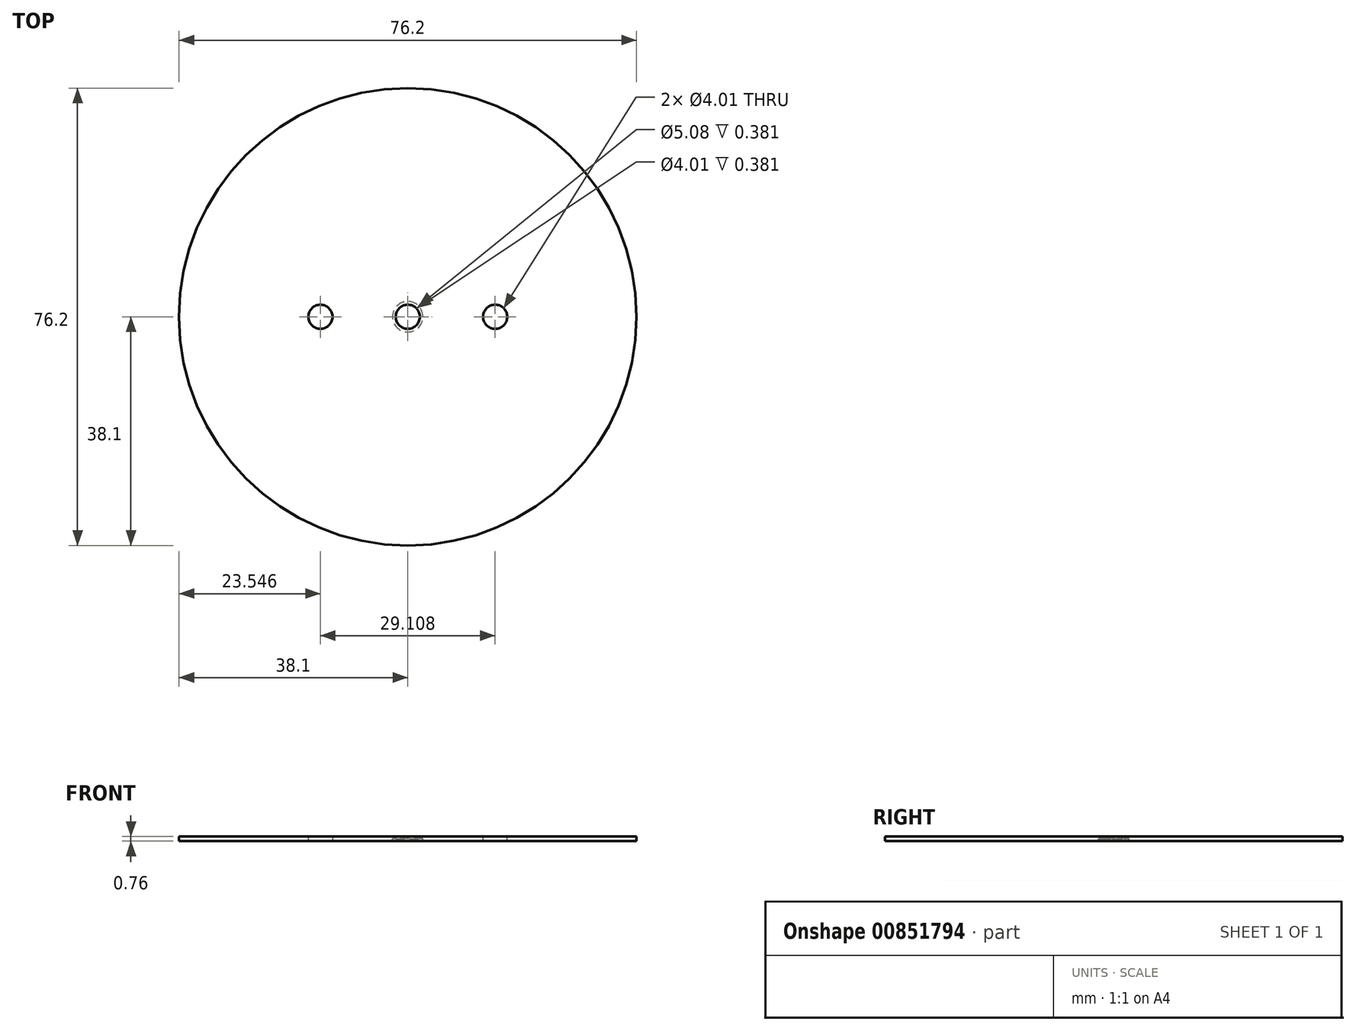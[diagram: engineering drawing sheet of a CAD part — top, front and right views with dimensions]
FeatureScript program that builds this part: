
annotation { "Feature Type Name" : "Feature", "Feature Type Description" : "" }
export const myFeature = defineFeature(function(context is Context, id is Id, definition is map)
    precondition{}
    {
        {
            var Q0;
            Q0=qCreatedBy(makeId("Top.planeOp"),FACE);
            var sketch = newSketch(context, id + "F0", { "sketchPlane" : qUnion([Q0])});
            skCircle(sketch, "E0", {"center": v(0, 0) * mm, "radius": 38.1 * mm});
            skPoint(sketch, "E1", {"position": v(-14.55, 0) * mm});
            skPoint(sketch, "E2.MirrorP", {"position": v(14.55, 0) * mm});
            skSolve(sketch);
        }
        {
            var Q0;
            Q0 = qSketchRegion(id + "F0", true);
            extrude(context, id + "F1", {"entities" : qUnion([Q0]), "endBound" : BoundingType.SYMMETRIC, "depth" : 0.76 * mm, "offsetDistance" : 25.4 * mm});
        }
        {
            var Q0;
            Q0=sQuery(id+"F0.wireOp",VERTEX,"E2.MirrorP");
            var Q1;
            Q1=makeQuery(id+"F1.opExtrude","SWEPT_BODY",BODY,{"disambiguationData":[OSD([sQuery(id+"F0.wireOp",EDGE,"E0")])]});
            hole(context, id + "F2", {"style" : HoleStyle.SIMPLE, "endStyle" : HoleEndStyle.THROUGH, "holeDiameter" : 4 * mm, "majorDiameter" : 6.35 * mm, "isTappedThrough" : true, "tappedDepth" : 12.7 * mm, "tapClearance" : 3, "locations" : qUnion([Q0]), "scope" : qUnion([Q1])});
        }
        {
            var Q0;
            Q0=sQuery(id+"F0.wireOp",VERTEX,"E2.MirrorP");
            var Q1;
            Q1=makeQuery(id+"F1.opExtrude","SWEPT_BODY",BODY,{"disambiguationData":[OSD([sQuery(id+"F0.wireOp",EDGE,"E0")])]});
            hole(context, id + "F3", {"style" : HoleStyle.SIMPLE, "endStyle" : HoleEndStyle.THROUGH, "oppositeDirection" : true, "holeDiameter" : 4 * mm, "majorDiameter" : 6.35 * mm, "isTappedThrough" : true, "tappedDepth" : 12.7 * mm, "tapClearance" : 3, "locations" : qUnion([Q0]), "scope" : qUnion([Q1])});
        }
        {
            var Q0;
            Q0=sQuery(id+"F0.wireOp",VERTEX,"E1");
            var Q1;
            Q1=makeQuery(id+"F1.opExtrude","SWEPT_BODY",BODY,{"disambiguationData":[OSD([sQuery(id+"F0.wireOp",EDGE,"E0")])]});
            hole(context, id + "F4", {"style" : HoleStyle.SIMPLE, "endStyle" : HoleEndStyle.THROUGH, "oppositeDirection" : true, "holeDiameter" : 4 * mm, "majorDiameter" : 6.35 * mm, "isTappedThrough" : true, "tappedDepth" : 12.7 * mm, "tapClearance" : 3, "locations" : qUnion([Q0]), "scope" : qUnion([Q1])});
        }
        {
            var Q0;
            Q0=sQuery(id+"F0.wireOp",VERTEX,"E1");
            var Q1;
            Q1=makeQuery(id+"F1.opExtrude","SWEPT_BODY",BODY,{"disambiguationData":[OSD([sQuery(id+"F0.wireOp",EDGE,"E0")])]});
            hole(context, id + "F5", {"style" : HoleStyle.SIMPLE, "endStyle" : HoleEndStyle.THROUGH, "holeDiameter" : 4 * mm, "majorDiameter" : 6.35 * mm, "isTappedThrough" : true, "tappedDepth" : 12.7 * mm, "tapClearance" : 3, "locations" : qUnion([Q0]), "scope" : qUnion([Q1])});
        }
        {
            var Q0;
            Q0=sQuery(id+"F0.wireOp",VERTEX,"E0.center");
            var Q1;
            Q1=makeQuery(id+"F1.opExtrude","SWEPT_BODY",BODY,{"disambiguationData":[OSD([sQuery(id+"F0.wireOp",EDGE,"E0")])]});
            hole(context, id + "F6", {"style" : HoleStyle.SIMPLE, "endStyle" : HoleEndStyle.THROUGH, "holeDiameter" : 5.08 * mm, "majorDiameter" : 6.35 * mm, "isTappedThrough" : true, "tappedDepth" : 12.7 * mm, "tapClearance" : 3, "locations" : qUnion([Q0]), "scope" : qUnion([Q1])});
        }
        {
            var Q0;
            Q0=sQuery(id+"F0.wireOp",VERTEX,"E0.center");
            var Q1;
            Q1=makeQuery(id+"F1.opExtrude","SWEPT_BODY",BODY,{"disambiguationData":[OSD([sQuery(id+"F0.wireOp",EDGE,"E0")])]});
            hole(context, id + "F7", {"style" : HoleStyle.SIMPLE, "endStyle" : HoleEndStyle.THROUGH, "oppositeDirection" : true, "holeDiameter" : 4 * mm, "majorDiameter" : 6.35 * mm, "isTappedThrough" : true, "tappedDepth" : 12.7 * mm, "tapClearance" : 3, "locations" : qUnion([Q0]), "scope" : qUnion([Q1])});
        }
    });
